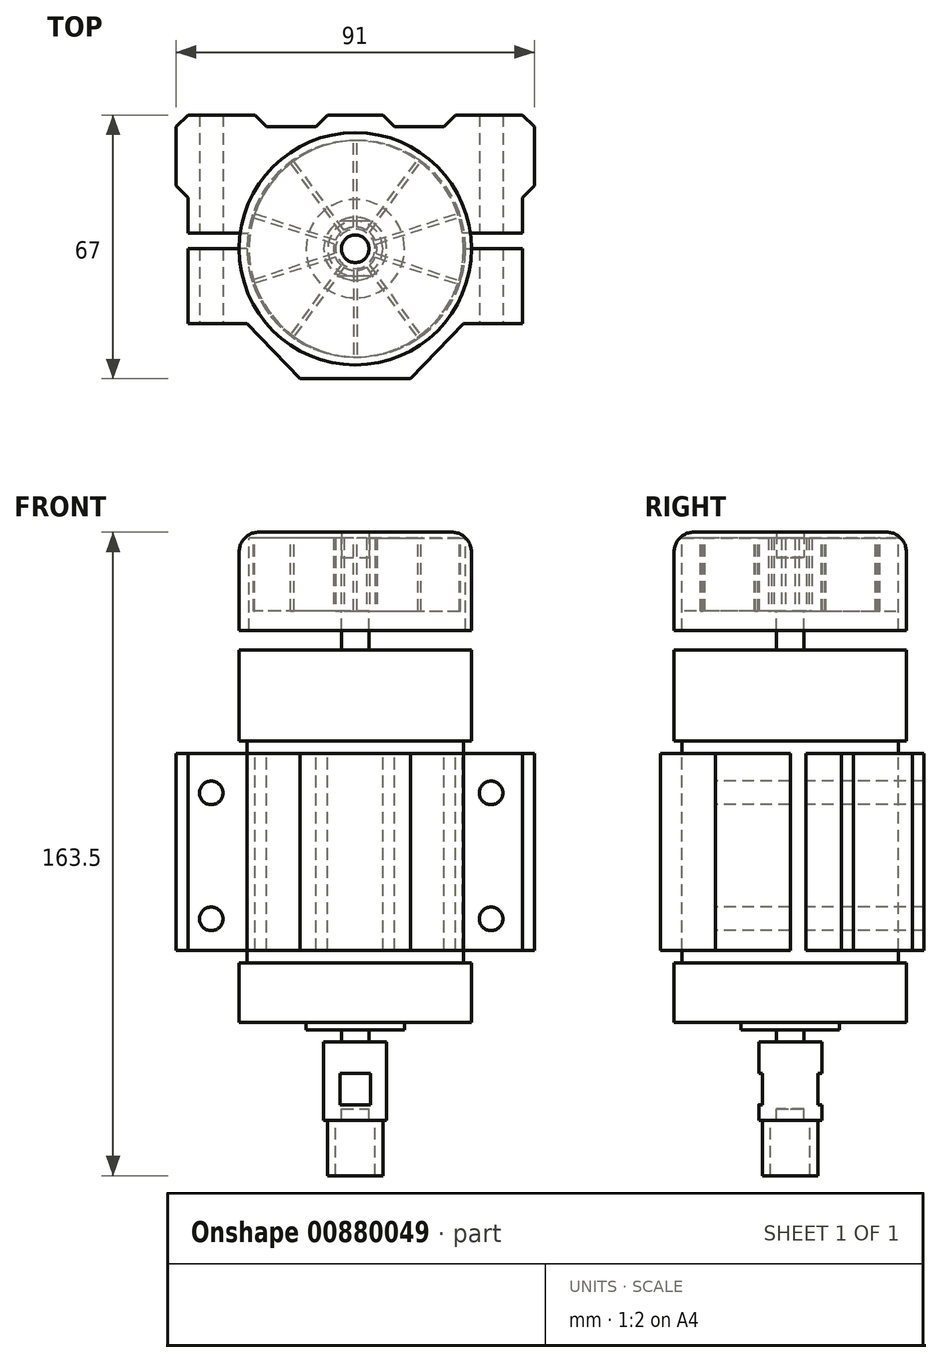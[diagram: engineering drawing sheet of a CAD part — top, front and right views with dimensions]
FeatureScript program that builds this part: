
annotation { "Feature Type Name" : "Feature", "Feature Type Description" : "" }
export const myFeature = defineFeature(function(context is Context, id is Id, definition is map)
    precondition{}
    {
        {
            var Q0;
            Q0=qCreatedBy(makeId("Top.planeOp"),FACE);
            var sketch = newSketch(context, id + "F0", { "sketchPlane" : qUnion([Q0])});
            skCircle(sketch, "E0", {"center": v(0, 0) * mm, "radius": 27.5 * mm});
            skLineSegment(sketch, "E1", {"start": v(-27.5, 0) * mm, "end": v(-42.5, 0) * mm});
            skLineSegment(sketch, "E2", {"start": v(-42.5, 0) * mm, "end": v(-42.5, -19) * mm});
            skLineSegment(sketch, "E3", {"start": v(-42.5, -19) * mm, "end": v(-27.5, -19) * mm});
            skLineSegment(sketch, "E4", {"start": v(-27.5, -19) * mm, "end": v(-14, -33) * mm});
            skLineSegment(sketch, "E5", {"start": v(-14, -33) * mm, "end": v(0, -33) * mm});
            skLineSegment(sketch, "E6.MirrorCS", {"start": v(14, -33) * mm, "end": v(0, -33) * mm});
            skLineSegment(sketch, "E7.MirrorCS", {"start": v(27.5, -19) * mm, "end": v(14, -33) * mm});
            skLineSegment(sketch, "E8.MirrorCS", {"start": v(42.5, -19) * mm, "end": v(27.5, -19) * mm});
            skLineSegment(sketch, "E9.MirrorCS", {"start": v(27.5, 0) * mm, "end": v(42.5, 0) * mm});
            skLineSegment(sketch, "E10.MirrorCS", {"start": v(42.5, 0) * mm, "end": v(42.5, -19) * mm});
            skLineSegment(sketch, "E11", {"start": v(-42.5, 4) * mm, "end": v(-42.5, 13) * mm});
            skLineSegment(sketch, "E12", {"start": v(-42.5, 13) * mm, "end": v(-45.5, 16) * mm});
            skLineSegment(sketch, "E13", {"start": v(-45.5, 16) * mm, "end": v(-45.5, 31) * mm});
            skLineSegment(sketch, "E14", {"start": v(-45.5, 31) * mm, "end": v(-42.5, 34) * mm});
            skLineSegment(sketch, "E15", {"start": v(-42.5, 34) * mm, "end": v(-25.5, 34) * mm});
            skLineSegment(sketch, "E16", {"start": v(-25.5, 34) * mm, "end": v(-22.5, 31) * mm});
            skLineSegment(sketch, "E17", {"start": v(-22.5, 31) * mm, "end": v(-10, 31) * mm});
            skLineSegment(sketch, "E18", {"start": v(-10, 31) * mm, "end": v(-7, 34) * mm});
            skLineSegment(sketch, "E19", {"start": v(-7, 34) * mm, "end": v(0, 34) * mm});
            skLineSegment(sketch, "E20", {"start": v(-42.5, 4) * mm, "end": v(-27.2, 4) * mm});
            skLineSegment(sketch, "E21.MirrorCS", {"start": v(25.5, 34) * mm, "end": v(22.5, 31) * mm});
            skLineSegment(sketch, "E22.MirrorCS", {"start": v(42.5, 34) * mm, "end": v(25.5, 34) * mm});
            skLineSegment(sketch, "E23.MirrorCS", {"start": v(45.5, 31) * mm, "end": v(42.5, 34) * mm});
            skLineSegment(sketch, "E24.MirrorCS", {"start": v(45.5, 16) * mm, "end": v(45.5, 31) * mm});
            skLineSegment(sketch, "E25.MirrorCS", {"start": v(7, 34) * mm, "end": v(0, 34) * mm});
            skLineSegment(sketch, "E26.MirrorCS", {"start": v(10, 31) * mm, "end": v(7, 34) * mm});
            skLineSegment(sketch, "E27.MirrorCS", {"start": v(22.5, 31) * mm, "end": v(10, 31) * mm});
            skLineSegment(sketch, "E28.MirrorCS", {"start": v(42.5, 13) * mm, "end": v(45.5, 16) * mm});
            skLineSegment(sketch, "E29.MirrorCS", {"start": v(42.5, 4) * mm, "end": v(42.5, 13) * mm});
            skLineSegment(sketch, "E30.MirrorCS", {"start": v(42.5, 4) * mm, "end": v(27.2, 4) * mm});
            skSolve(sketch);
        }
        {
            var Q0;
            Q0=makeQuery(id+"F0.imprint","IMPRINT",FACE,{"disambiguationData":[TD([[makeQuery(id+"F0.imprint","IMPRINT",EDGE,{"derivedFrom":sQuery(id+"F0.wireOp",EDGE,"E0")}),1.0]])]});
            extrude(context, id + "F1", {"entities" : qUnion([Q0]), "endBound" : BoundingType.SYMMETRIC, "oppositeDirection" : true, "depth" : 56.5 * mm});
        }
        {
            var Q0;
            Q0=makeQuery(id+"F1.opExtrude","CAP_FACE",FACE,{"disambiguationData":[OSD([sQuery(id+"F0.wireOp",EDGE,"E0")])],"isStart":true});
            var sketch = newSketch(context, id + "F2", { "sketchPlane" : qUnion([Q0])});
            skCircle(sketch, "E31.0", {"center": v(0, 0) * mm, "radius": 29.5 * mm});
            skSolve(sketch);
        }
        {
            var Q0;
            Q0=makeQuery(id+"F2.imprint","IMPRINT",FACE,{"disambiguationData":[TD([[makeQuery(id+"F2.imprint","IMPRINT",EDGE,{"derivedFrom":sQuery(id+"F2.wireOp",EDGE,"E31.0")}),1.0]])]});
            var Q1;
            Q1=makeQuery(id+"F2.imprint","IMPRINT",FACE,{"disambiguationData":[TD([[makeQuery(id+"F2.imprint","IMPRINT",EDGE,{"derivedFrom":makeQuery(id+"F1.opExtrude","CAP_EDGE",EDGE,{"disambiguationData":[OSD([sQuery(id+"F0.wireOp",EDGE,"E0")])],"isStart":true})}),1.0]])]});
            extrude(context, id + "F3", {"entities" : qUnion([Q0, Q1]), "operationType" : NewBodyOperationType.ADD, "depth" : 23 * mm});
        }
        {
            var Q0;
            Q0=makeQuery(id+"F1.opExtrude","CAP_FACE",FACE,{"disambiguationData":[OSD([sQuery(id+"F0.wireOp",EDGE,"E0")])],"isStart":false});
            var sketch = newSketch(context, id + "F4", { "sketchPlane" : qUnion([Q0])});
            skCircle(sketch, "E32.0", {"center": v(0, 0) * mm, "radius": 29.5 * mm});
            skSolve(sketch);
        }
        {
            var Q0;
            Q0=makeQuery(id+"F4.imprint","IMPRINT",FACE,{"disambiguationData":[TD([[makeQuery(id+"F4.imprint","IMPRINT",EDGE,{"derivedFrom":sQuery(id+"F4.wireOp",EDGE,"E32.0")}),1.0]])]});
            var Q1;
            Q1=makeQuery(id+"F4.imprint","IMPRINT",FACE,{"disambiguationData":[TD([[makeQuery(id+"F4.imprint","IMPRINT",EDGE,{"derivedFrom":makeQuery(id+"F1.opExtrude","CAP_EDGE",EDGE,{"disambiguationData":[OSD([sQuery(id+"F0.wireOp",EDGE,"E0")])],"isStart":false})}),-1.0]])]});
            extrude(context, id + "F5", {"entities" : qUnion([Q0, Q1]), "operationType" : NewBodyOperationType.ADD, "depth" : 15 * mm});
        }
        {
            var Q0;
            Q0=makeQuery(id+"F5.opExtrude","CAP_FACE",FACE,{"disambiguationData":[OSD([sQuery(id+"F4.wireOp",EDGE,"E32.0")])],"isStart":false});
            var sketch = newSketch(context, id + "F6", { "sketchPlane" : qUnion([Q0])});
            skCircle(sketch, "E33", {"center": v(0, 0) * mm, "radius": 12.5 * mm});
            skSolve(sketch);
        }
        {
            var Q0;
            Q0=makeQuery(id+"F6.imprint","IMPRINT",FACE,{"disambiguationData":[TD([[makeQuery(id+"F6.imprint","IMPRINT",EDGE,{"derivedFrom":sQuery(id+"F6.wireOp",EDGE,"E33")}),1.0]])]});
            extrude(context, id + "F7", {"entities" : qUnion([Q0]), "operationType" : NewBodyOperationType.ADD, "depth" : 2 * mm});
        }
        {
            var Q0;
            Q0=makeQuery(id+"F7.opExtrude","CAP_FACE",FACE,{"disambiguationData":[OSD([sQuery(id+"F6.wireOp",EDGE,"E33")])],"isStart":false});
            var sketch = newSketch(context, id + "F8", { "sketchPlane" : qUnion([Q0])});
            skCircle(sketch, "E34", {"center": v(0, 0) * mm, "radius": 3.5 * mm});
            skSolve(sketch);
        }
        {
            var Q0;
            Q0=makeQuery(id+"F8.imprint","IMPRINT",FACE,{"disambiguationData":[TD([[makeQuery(id+"F8.imprint","IMPRINT",EDGE,{"derivedFrom":sQuery(id+"F8.wireOp",EDGE,"E34")}),1.0]])]});
            extrude(context, id + "F9", {"entities" : qUnion([Q0]), "operationType" : NewBodyOperationType.ADD, "depth" : 20 * mm, "hasSecondDirection" : true, "secondDirectionOppositeDirection" : true, "secondDirectionDepth" : 120 * mm});
        }
        {
            var Q0;
            Q0=makeQuery(id+"F7.opExtrude","CAP_FACE",FACE,{"disambiguationData":[OSD([sQuery(id+"F6.wireOp",EDGE,"E33")])],"isStart":false});
            cPlane(context, id + "F10", {"entities" : qUnion([Q0]), "cplaneType" : CPlaneType.OFFSET, "offset" : 3 * mm, "width" : 150 * mm, "height" : 150 * mm});
        }
        {
            var Q0;
            Q0=qCreatedBy(id+"F10.planeOp",FACE);
            var sketch = newSketch(context, id + "F11", { "sketchPlane" : qUnion([Q0])});
            skCircle(sketch, "E35", {"center": v(0, 0) * mm, "radius": 8 * mm});
            skCircle(sketch, "E36", {"center": v(0, 0) * mm, "radius": 3.5 * mm});
            skSolve(sketch);
        }
        {
            var Q0;
            Q0=makeQuery(id+"F11.imprint","IMPRINT",FACE,{"disambiguationData":[TD([[makeQuery(id+"F11.imprint","IMPRINT",EDGE,{"derivedFrom":sQuery(id+"F11.wireOp",EDGE,"E35")}),1.0]])]});
            extrude(context, id + "F12", {"entities" : qUnion([Q0]), "operationType" : NewBodyOperationType.ADD, "depth" : 20 * mm});
        }
        {
            var Q0;
            Q0=qCreatedBy(makeId("Right.planeOp"),FACE);
            var sketch = newSketch(context, id + "F13", { "sketchPlane" : qUnion([Q0])});
            skLineSegment(sketch, "E37.bottom", {"start": v(12.32, -56.25) * mm, "end": v(7, -56.25) * mm});
            skLineSegment(sketch, "E37.top", {"start": v(12.32, -64.25) * mm, "end": v(7, -64.25) * mm});
            skLineSegment(sketch, "E37.left", {"start": v(12.32, -56.25) * mm, "end": v(12.32, -64.25) * mm});
            skLineSegment(sketch, "E37.right", {"start": v(7, -56.25) * mm, "end": v(7, -64.25) * mm});
            skLineSegment(sketch, "E38", {"start": v(0, -59.62) * mm, "end": v(0, -108.48) * mm, "construction": true});
            skLineSegment(sketch, "E39.MirrorCS", {"start": v(-12.32, -56.25) * mm, "end": v(-7, -56.25) * mm});
            skLineSegment(sketch, "E40.MirrorCS", {"start": v(-12.32, -64.25) * mm, "end": v(-7, -64.25) * mm});
            skLineSegment(sketch, "E41.MirrorCS", {"start": v(-12.32, -56.25) * mm, "end": v(-12.32, -64.25) * mm});
            skLineSegment(sketch, "E42.MirrorCS", {"start": v(-7, -56.25) * mm, "end": v(-7, -64.25) * mm});
            skSolve(sketch);
        }
        {
            var Q0;
            Q0=makeQuery(id+"F13.imprint","IMPRINT",FACE,{"disambiguationData":[TD([[makeQuery(id+"F13.imprint","IMPRINT",EDGE,{"derivedFrom":sQuery(id+"F13.wireOp",EDGE,"E37.bottom")}),1.0]])]});
            var Q1;
            Q1=makeQuery(id+"F13.imprint","IMPRINT",FACE,{"disambiguationData":[TD([[makeQuery(id+"F13.imprint","IMPRINT",EDGE,{"derivedFrom":sQuery(id+"F13.wireOp",EDGE,"E39.MirrorCS")}),-1.0]])]});
            extrude(context, id + "F14", {"entities" : qUnion([Q0, Q1]), "operationType" : NewBodyOperationType.REMOVE, "endBound" : BoundingType.SYMMETRIC, "depth" : 10 * mm});
        }
        {
            var Q0;
            Q0=makeQuery(id+"F12.opExtrude","CAP_FACE",FACE,{"disambiguationData":[OSD([sQuery(id+"F11.wireOp",EDGE,"E35"),sQuery(id+"F11.wireOp",EDGE,"E36")])],"isStart":false});
            var sketch = newSketch(context, id + "F15", { "sketchPlane" : qUnion([Q0])});
            skCircle(sketch, "E43", {"center": v(0, 0) * mm, "radius": 7 * mm});
            skCircle(sketch, "E44.0", {"center": v(0, 0) * mm, "radius": 5 * mm});
            skSolve(sketch);
        }
        {
            var Q0;
            Q0=makeQuery(id+"F15.imprint","IMPRINT",FACE,{"disambiguationData":[TD([[makeQuery(id+"F15.imprint","IMPRINT",EDGE,{"derivedFrom":sQuery(id+"F15.wireOp",EDGE,"E43")}),1.0]])]});
            extrude(context, id + "F16", {"entities" : qUnion([Q0]), "operationType" : NewBodyOperationType.ADD, "depth" : 14 * mm});
        }
        {
            var Q0;
            Q0=makeQuery(id+"F3.opExtrude","CAP_FACE",FACE,{"disambiguationData":[OSD([sQuery(id+"F2.wireOp",EDGE,"E31.0")])],"isStart":false});
            cPlane(context, id + "F17", {"entities" : qUnion([Q0]), "cplaneType" : CPlaneType.OFFSET, "offset" : 10 * mm, "width" : 150 * mm, "height" : 150 * mm});
        }
        {
            var Q0;
            Q0=qCreatedBy(id+"F17.planeOp",FACE);
            var sketch = newSketch(context, id + "F18", { "sketchPlane" : qUnion([Q0])});
            skLineSegment(sketch, "E45.bottom", {"start": v(-0.5, -3.78) * mm, "end": v(0.5, -3.78) * mm});
            skLineSegment(sketch, "E45.top", {"start": v(-0.5, -29.13) * mm, "end": v(0.5, -29.13) * mm});
            skLineSegment(sketch, "E45.left", {"start": v(-0.5, -5.48) * mm, "end": v(-0.5, -29.13) * mm});
            skLineSegment(sketch, "E45.right", {"start": v(0.5, -5.48) * mm, "end": v(0.5, -29.13) * mm});
            skLineSegment(sketch, "E46.1.0", {"start": v(3.62, -4.14) * mm, "end": v(17.53, -23.27) * mm});
            skLineSegment(sketch, "E46.1.1", {"start": v(2.81, -4.73) * mm, "end": v(16.72, -23.86) * mm});
            skLineSegment(sketch, "E46.1.2", {"start": v(16.72, -23.86) * mm, "end": v(17.53, -23.27) * mm});
            skLineSegment(sketch, "E46.1.3", {"start": v(1.82, -3.35) * mm, "end": v(2.63, -2.76) * mm});
            skLineSegment(sketch, "E46.2.0", {"start": v(5.36, -1.22) * mm, "end": v(27.86, -8.53) * mm});
            skLineSegment(sketch, "E46.2.1", {"start": v(5.05, -2.17) * mm, "end": v(27.55, -9.48) * mm});
            skLineSegment(sketch, "E46.2.2", {"start": v(27.55, -9.48) * mm, "end": v(27.86, -8.53) * mm});
            skLineSegment(sketch, "E46.2.3", {"start": v(3.44, -1.64) * mm, "end": v(3.75, -0.7) * mm});
            skLineSegment(sketch, "E46.3.0", {"start": v(5.05, 2.17) * mm, "end": v(27.55, 9.48) * mm});
            skLineSegment(sketch, "E46.3.1", {"start": v(5.36, 1.22) * mm, "end": v(27.86, 8.53) * mm});
            skLineSegment(sketch, "E46.3.2", {"start": v(27.86, 8.53) * mm, "end": v(27.55, 9.48) * mm});
            skLineSegment(sketch, "E46.3.3", {"start": v(3.75, 0.7) * mm, "end": v(3.44, 1.64) * mm});
            skLineSegment(sketch, "E46.4.0", {"start": v(2.81, 4.73) * mm, "end": v(16.72, 23.86) * mm});
            skLineSegment(sketch, "E46.4.1", {"start": v(3.62, 4.14) * mm, "end": v(17.53, 23.27) * mm});
            skLineSegment(sketch, "E46.4.2", {"start": v(17.53, 23.27) * mm, "end": v(16.72, 23.86) * mm});
            skLineSegment(sketch, "E46.4.3", {"start": v(2.63, 2.76) * mm, "end": v(1.82, 3.35) * mm});
            skLineSegment(sketch, "E46.5.0", {"start": v(-0.5, 5.48) * mm, "end": v(-0.5, 29.13) * mm});
            skLineSegment(sketch, "E46.5.1", {"start": v(0.5, 5.48) * mm, "end": v(0.5, 29.13) * mm});
            skLineSegment(sketch, "E46.5.2", {"start": v(0.5, 29.13) * mm, "end": v(-0.5, 29.13) * mm});
            skLineSegment(sketch, "E46.5.3", {"start": v(0.5, 3.78) * mm, "end": v(-0.5, 3.78) * mm});
            skLineSegment(sketch, "E46.6.0", {"start": v(-3.62, 4.14) * mm, "end": v(-17.53, 23.27) * mm});
            skLineSegment(sketch, "E46.6.1", {"start": v(-2.81, 4.73) * mm, "end": v(-16.72, 23.86) * mm});
            skLineSegment(sketch, "E46.6.2", {"start": v(-16.72, 23.86) * mm, "end": v(-17.53, 23.27) * mm});
            skLineSegment(sketch, "E46.6.3", {"start": v(-1.82, 3.35) * mm, "end": v(-2.63, 2.76) * mm});
            skLineSegment(sketch, "E46.7.0", {"start": v(-5.36, 1.22) * mm, "end": v(-27.86, 8.53) * mm});
            skLineSegment(sketch, "E46.7.1", {"start": v(-5.05, 2.17) * mm, "end": v(-27.55, 9.48) * mm});
            skLineSegment(sketch, "E46.7.2", {"start": v(-27.55, 9.48) * mm, "end": v(-27.86, 8.53) * mm});
            skLineSegment(sketch, "E46.7.3", {"start": v(-3.44, 1.64) * mm, "end": v(-3.75, 0.7) * mm});
            skLineSegment(sketch, "E46.8.0", {"start": v(-5.05, -2.17) * mm, "end": v(-27.55, -9.48) * mm});
            skLineSegment(sketch, "E46.8.1", {"start": v(-5.36, -1.22) * mm, "end": v(-27.86, -8.53) * mm});
            skLineSegment(sketch, "E46.8.2", {"start": v(-27.86, -8.53) * mm, "end": v(-27.55, -9.48) * mm});
            skLineSegment(sketch, "E46.8.3", {"start": v(-3.75, -0.7) * mm, "end": v(-3.44, -1.64) * mm});
            skLineSegment(sketch, "E46.9.0", {"start": v(-2.81, -4.73) * mm, "end": v(-16.72, -23.86) * mm});
            skLineSegment(sketch, "E46.9.1", {"start": v(-3.62, -4.14) * mm, "end": v(-17.53, -23.27) * mm});
            skLineSegment(sketch, "E46.9.2", {"start": v(-17.53, -23.27) * mm, "end": v(-16.72, -23.86) * mm});
            skLineSegment(sketch, "E46.9.3", {"start": v(-2.63, -2.76) * mm, "end": v(-1.82, -3.35) * mm});
            skPoint(sketch, "E46.center", {"position": v(0, 0) * mm});
            skCircle(sketch, "E47", {"center": v(0, 0) * mm, "radius": 3.5 * mm});
            skArc(sketch, "E48", {"start": v(-5.36, 1.22) * mm, "mid": v(-5.5, 0) * mm, "end": v(-5.36, -1.22) * mm});
            skArc(sketch, "E49.trimOffspring", {"start": v(-3.62, 4.14) * mm, "mid": v(-4.45, 3.23) * mm, "end": v(-5.05, 2.17) * mm});
            skArc(sketch, "E50.trimOffspring", {"start": v(-0.5, 5.48) * mm, "mid": v(-1.7, 5.23) * mm, "end": v(-2.81, 4.73) * mm});
            skArc(sketch, "E51.trimOffspring", {"start": v(2.81, 4.73) * mm, "mid": v(1.7, 5.23) * mm, "end": v(0.5, 5.48) * mm});
            skArc(sketch, "E52.trimOffspring", {"start": v(5.05, 2.17) * mm, "mid": v(4.45, 3.23) * mm, "end": v(3.62, 4.14) * mm});
            skArc(sketch, "E53.trimOffspring", {"start": v(5.36, -1.22) * mm, "mid": v(5.5, 0) * mm, "end": v(5.36, 1.22) * mm});
            skArc(sketch, "E54.trimOffspring", {"start": v(3.62, -4.14) * mm, "mid": v(4.45, -3.23) * mm, "end": v(5.05, -2.17) * mm});
            skArc(sketch, "E55.trimOffspring", {"start": v(0.5, -5.48) * mm, "mid": v(1.7, -5.23) * mm, "end": v(2.81, -4.73) * mm});
            skArc(sketch, "E56.trimOffspring", {"start": v(-2.81, -4.73) * mm, "mid": v(-1.7, -5.23) * mm, "end": v(-0.5, -5.48) * mm});
            skArc(sketch, "E57.trimOffspring", {"start": v(-5.05, -2.17) * mm, "mid": v(-4.45, -3.23) * mm, "end": v(-3.62, -4.14) * mm});
            skSolve(sketch);
        }
        {
            var Q0;
            Q0=makeQuery(id+"F18.imprint","IMPRINT",FACE,{"disambiguationData":[TD([[makeQuery(id+"F18.imprint","IMPRINT",EDGE,{"derivedFrom":sQuery(id+"F18.wireOp",EDGE,"E45.top")}),1.0]])]});
            extrude(context, id + "F19", {"entities" : qUnion([Q0]), "operationType" : NewBodyOperationType.ADD, "depth" : 20 * mm});
        }
        {
            var Q0;
            Q0=makeQuery(id+"F19.opExtrude","CAP_FACE",FACE,{"disambiguationData":[OSD([sQuery(id+"F18.wireOp",EDGE,"E45.top"),sQuery(id+"F18.wireOp",EDGE,"E45.left"),sQuery(id+"F18.wireOp",EDGE,"E45.right"),sQuery(id+"F18.wireOp",EDGE,"E46.1.0"),sQuery(id+"F18.wireOp",EDGE,"E46.1.1"),sQuery(id+"F18.wireOp",EDGE,"E46.1.2"),sQuery(id+"F18.wireOp",EDGE,"E46.2.0"),sQuery(id+"F18.wireOp",EDGE,"E46.2.1"),sQuery(id+"F18.wireOp",EDGE,"E46.2.2"),sQuery(id+"F18.wireOp",EDGE,"E46.3.0"),sQuery(id+"F18.wireOp",EDGE,"E46.3.1"),sQuery(id+"F18.wireOp",EDGE,"E46.3.2"),sQuery(id+"F18.wireOp",EDGE,"E46.4.0"),sQuery(id+"F18.wireOp",EDGE,"E46.4.1"),sQuery(id+"F18.wireOp",EDGE,"E46.4.2"),sQuery(id+"F18.wireOp",EDGE,"E46.5.0"),sQuery(id+"F18.wireOp",EDGE,"E46.5.1"),sQuery(id+"F18.wireOp",EDGE,"E46.5.2"),sQuery(id+"F18.wireOp",EDGE,"E46.6.0"),sQuery(id+"F18.wireOp",EDGE,"E46.6.1"),sQuery(id+"F18.wireOp",EDGE,"E46.6.2"),sQuery(id+"F18.wireOp",EDGE,"E46.7.0"),sQuery(id+"F18.wireOp",EDGE,"E46.7.1"),sQuery(id+"F18.wireOp",EDGE,"E46.7.2"),sQuery(id+"F18.wireOp",EDGE,"E46.8.0"),sQuery(id+"F18.wireOp",EDGE,"E46.8.1"),sQuery(id+"F18.wireOp",EDGE,"E46.8.2"),sQuery(id+"F18.wireOp",EDGE,"E46.9.0"),sQuery(id+"F18.wireOp",EDGE,"E46.9.1"),sQuery(id+"F18.wireOp",EDGE,"E46.9.2"),sQuery(id+"F18.wireOp",EDGE,"E47"),sQuery(id+"F18.wireOp",EDGE,"E48"),sQuery(id+"F18.wireOp",EDGE,"E49.trimOffspring"),sQuery(id+"F18.wireOp",EDGE,"E50.trimOffspring"),sQuery(id+"F18.wireOp",EDGE,"E51.trimOffspring"),sQuery(id+"F18.wireOp",EDGE,"E52.trimOffspring"),sQuery(id+"F18.wireOp",EDGE,"E53.trimOffspring"),sQuery(id+"F18.wireOp",EDGE,"E54.trimOffspring"),sQuery(id+"F18.wireOp",EDGE,"E55.trimOffspring"),sQuery(id+"F18.wireOp",EDGE,"E56.trimOffspring"),sQuery(id+"F18.wireOp",EDGE,"E57.trimOffspring")])],"isStart":false});
            var sketch = newSketch(context, id + "F20", { "sketchPlane" : qUnion([Q0])});
            skCircle(sketch, "E58", {"center": v(0, 0) * mm, "radius": 29.5 * mm});
            skSolve(sketch);
        }
        {
            var Q0;
            Q0=makeQuery(id+"F20.imprint","IMPRINT",FACE,{"disambiguationData":[TD([[makeQuery(id+"F20.imprint","IMPRINT",EDGE,{"derivedFrom":sQuery(id+"F20.wireOp",EDGE,"E58")}),1.0]])]});
            extrude(context, id + "F21", {"entities" : qUnion([Q0]), "operationType" : NewBodyOperationType.ADD, "oppositeDirection" : true, "depth" : 1.5 * mm});
        }
        {
            var Q0;
            {var subQ0=sQuery(id+"F18.wireOp",EDGE,"E57.trimOffspring");var subQ1=sQuery(id+"F18.wireOp",EDGE,"E56.trimOffspring");var subQ2=sQuery(id+"F18.wireOp",EDGE,"E55.trimOffspring");var subQ3=sQuery(id+"F18.wireOp",EDGE,"E54.trimOffspring");var subQ4=sQuery(id+"F18.wireOp",EDGE,"E53.trimOffspring");var subQ5=sQuery(id+"F18.wireOp",EDGE,"E52.trimOffspring");var subQ6=sQuery(id+"F18.wireOp",EDGE,"E51.trimOffspring");var subQ7=sQuery(id+"F18.wireOp",EDGE,"E50.trimOffspring");var subQ8=sQuery(id+"F18.wireOp",EDGE,"E49.trimOffspring");var subQ9=sQuery(id+"F18.wireOp",EDGE,"E48");var subQ10=sQuery(id+"F18.wireOp",EDGE,"E46.9.2");var subQ11=sQuery(id+"F18.wireOp",EDGE,"E46.9.1");var subQ12=sQuery(id+"F18.wireOp",EDGE,"E46.9.0");var subQ13=sQuery(id+"F18.wireOp",EDGE,"E46.8.2");var subQ14=sQuery(id+"F18.wireOp",EDGE,"E46.8.1");var subQ15=sQuery(id+"F18.wireOp",EDGE,"E46.8.0");var subQ16=sQuery(id+"F18.wireOp",EDGE,"E46.7.2");var subQ17=sQuery(id+"F18.wireOp",EDGE,"E46.7.1");var subQ18=sQuery(id+"F18.wireOp",EDGE,"E46.7.0");var subQ19=sQuery(id+"F18.wireOp",EDGE,"E46.6.2");var subQ20=sQuery(id+"F18.wireOp",EDGE,"E46.6.1");var subQ21=sQuery(id+"F18.wireOp",EDGE,"E46.6.0");var subQ22=sQuery(id+"F18.wireOp",EDGE,"E46.5.2");var subQ23=sQuery(id+"F18.wireOp",EDGE,"E46.5.1");var subQ24=sQuery(id+"F18.wireOp",EDGE,"E46.5.0");var subQ25=sQuery(id+"F18.wireOp",EDGE,"E46.4.2");var subQ26=sQuery(id+"F18.wireOp",EDGE,"E46.4.1");var subQ27=sQuery(id+"F18.wireOp",EDGE,"E46.4.0");var subQ28=sQuery(id+"F18.wireOp",EDGE,"E46.3.2");var subQ29=sQuery(id+"F18.wireOp",EDGE,"E46.3.1");var subQ30=sQuery(id+"F18.wireOp",EDGE,"E46.3.0");var subQ31=sQuery(id+"F18.wireOp",EDGE,"E46.2.2");var subQ32=sQuery(id+"F18.wireOp",EDGE,"E46.2.1");var subQ33=sQuery(id+"F18.wireOp",EDGE,"E46.2.0");var subQ34=sQuery(id+"F18.wireOp",EDGE,"E46.1.2");var subQ35=sQuery(id+"F18.wireOp",EDGE,"E46.1.1");var subQ36=sQuery(id+"F18.wireOp",EDGE,"E46.1.0");var subQ37=sQuery(id+"F18.wireOp",EDGE,"E45.right");var subQ38=sQuery(id+"F18.wireOp",EDGE,"E45.left");var subQ39=sQuery(id+"F18.wireOp",EDGE,"E45.top");Q0=makeQuery(id+"F21.boolean.opBoolean","MERGE",FACE,{"derivedFrom":[makeQuery(id+"F19.opExtrude","CAP_FACE",FACE,{"disambiguationData":[OSD([subQ39,subQ38,subQ37,subQ36,subQ35,subQ34,subQ33,subQ32,subQ31,subQ30,subQ29,subQ28,subQ27,subQ26,subQ25,subQ24,subQ23,subQ22,subQ21,subQ20,subQ19,subQ18,subQ17,subQ16,subQ15,subQ14,subQ13,subQ12,subQ11,subQ10,sQuery(id+"F18.wireOp",EDGE,"E47"),subQ9,subQ8,subQ7,subQ6,subQ5,subQ4,subQ3,subQ2,subQ1,subQ0])],"isStart":false}),makeQuery(id+"F21.opExtrude","CAP_FACE",FACE,{"disambiguationData":[OSD([subQ39,subQ38,subQ37,subQ36,subQ35,subQ34,subQ33,subQ32,subQ31,subQ30,subQ29,subQ28,subQ27,subQ26,subQ25,subQ24,subQ23,subQ22,subQ21,subQ20,subQ19,subQ18,subQ17,subQ16,subQ15,subQ14,subQ13,subQ12,subQ11,subQ10,subQ9,subQ8,subQ7,subQ6,subQ5,subQ4,subQ3,subQ2,subQ1,subQ0,sQuery(id+"F20.wireOp",EDGE,"E58")])],"isStart":true})]});}
            var sketch = newSketch(context, id + "F22", { "sketchPlane" : qUnion([Q0])});
            skCircle(sketch, "E59", {"center": v(0.5, 0) * mm, "radius": 27.5 * mm});
            skSolve(sketch);
        }
        {
            var Q0;
            Q0=makeQuery(id+"F22.imprint","IMPRINT",FACE,{"disambiguationData":[TD([[makeQuery(id+"F22.imprint","IMPRINT",EDGE,{"derivedFrom":sQuery(id+"F22.wireOp",EDGE,"E59")}),-1.0]])]});
            extrude(context, id + "F23", {"entities" : qUnion([Q0]), "operationType" : NewBodyOperationType.ADD, "oppositeDirection" : true, "depth" : 25 * mm});
        }
        {
            var Q0;
            Q0=makeQuery(id+"F21.opExtrude","CAP_EDGE",EDGE,{"disambiguationData":[OSD([sQuery(id+"F20.wireOp",EDGE,"E58")])],"isStart":true});
            fillet(context, id + "F24", {"entities" : qUnion([Q0]), "radius" : 5 * mm, "tangentPropagation" : true, "allowEdgeOverflow" : false});
        }
        {
            var Q0;
            {var subQ0=sQuery(id+"F0.wireOp",EDGE,"E1");Q0=makeQuery(id+"F0.imprint","IMPRINT",FACE,{"disambiguationData":[TD([[makeQuery(id+"F0.imprint","IMPRINT",EDGE,{"derivedFrom":subQ0}),1.0]])]});}
            var Q1;
            Q1=makeQuery(id+"F0.imprint","IMPRINT",FACE,{"disambiguationData":[TD([[makeQuery(id+"F0.imprint","IMPRINT",EDGE,{"derivedFrom":sQuery(id+"F0.wireOp",EDGE,"E11")}),-1.0]])]});
            extrude(context, id + "F25", {"entities" : qUnion([Q0, Q1]), "endBound" : BoundingType.SYMMETRIC, "oppositeDirection" : true, "depth" : 50 * mm});
        }
        {
            var Q0;
            Q0=makeQuery(id+"F25.opExtrude","SWEPT_FACE",FACE,{"disambiguationData":[OSD([sQuery(id+"F0.wireOp",EDGE,"E8.MirrorCS")])]});
            var sketch = newSketch(context, id + "F26", { "sketchPlane" : qUnion([Q0])});
            skPoint(sketch, "E60", {"position": v(34.5, 15) * mm});
            skPoint(sketch, "E61", {"position": v(34.5, -17) * mm});
            skPoint(sketch, "E62", {"position": v(-36.6, 15) * mm});
            skPoint(sketch, "E63", {"position": v(-36.6, -17) * mm});
            skSolve(sketch);
        }
        {
            var Q0;
            Q0=sQuery(id+"F26.wireOp",VERTEX,"E62");
            var Q1;
            Q1=sQuery(id+"F26.wireOp",VERTEX,"E63");
            var Q2;
            Q2=sQuery(id+"F26.wireOp",VERTEX,"E60");
            var Q3;
            Q3=sQuery(id+"F26.wireOp",VERTEX,"E61");
            var Q4;
            Q4=makeQuery(id+"F25.opExtrude","SWEPT_BODY",BODY,{"disambiguationData":[OSD([sQuery(id+"F0.wireOp",EDGE,"E0"),sQuery(id+"F0.wireOp",EDGE,"E1"),sQuery(id+"F0.wireOp",EDGE,"E2"),sQuery(id+"F0.wireOp",EDGE,"E3"),sQuery(id+"F0.wireOp",EDGE,"E4"),sQuery(id+"F0.wireOp",EDGE,"E5"),sQuery(id+"F0.wireOp",EDGE,"E6.MirrorCS"),sQuery(id+"F0.wireOp",EDGE,"E7.MirrorCS"),sQuery(id+"F0.wireOp",EDGE,"E8.MirrorCS"),sQuery(id+"F0.wireOp",EDGE,"E9.MirrorCS"),sQuery(id+"F0.wireOp",EDGE,"E10.MirrorCS")])]});
            var Q5;
            Q5=makeQuery(id+"F25.opExtrude","SWEPT_BODY",BODY,{"disambiguationData":[OSD([sQuery(id+"F0.wireOp",EDGE,"E0"),sQuery(id+"F0.wireOp",EDGE,"E11"),sQuery(id+"F0.wireOp",EDGE,"E12"),sQuery(id+"F0.wireOp",EDGE,"E13"),sQuery(id+"F0.wireOp",EDGE,"E14"),sQuery(id+"F0.wireOp",EDGE,"E15"),sQuery(id+"F0.wireOp",EDGE,"E16"),sQuery(id+"F0.wireOp",EDGE,"E17"),sQuery(id+"F0.wireOp",EDGE,"E18"),sQuery(id+"F0.wireOp",EDGE,"E19"),sQuery(id+"F0.wireOp",EDGE,"E20"),sQuery(id+"F0.wireOp",EDGE,"E21.MirrorCS"),sQuery(id+"F0.wireOp",EDGE,"E22.MirrorCS"),sQuery(id+"F0.wireOp",EDGE,"E23.MirrorCS"),sQuery(id+"F0.wireOp",EDGE,"E24.MirrorCS"),sQuery(id+"F0.wireOp",EDGE,"E25.MirrorCS"),sQuery(id+"F0.wireOp",EDGE,"E26.MirrorCS"),sQuery(id+"F0.wireOp",EDGE,"E27.MirrorCS"),sQuery(id+"F0.wireOp",EDGE,"E28.MirrorCS"),sQuery(id+"F0.wireOp",EDGE,"E29.MirrorCS"),sQuery(id+"F0.wireOp",EDGE,"E30.MirrorCS")])]});
            hole(context, id + "F27", {"style" : HoleStyle.SIMPLE, "endStyle" : HoleEndStyle.THROUGH, "holeDiameter" : 6 * mm, "locations" : qUnion([Q0, Q1, Q2, Q3]), "scope" : qUnion([Q4, Q5]), "isTappedThrough" : true});
        }
    });
